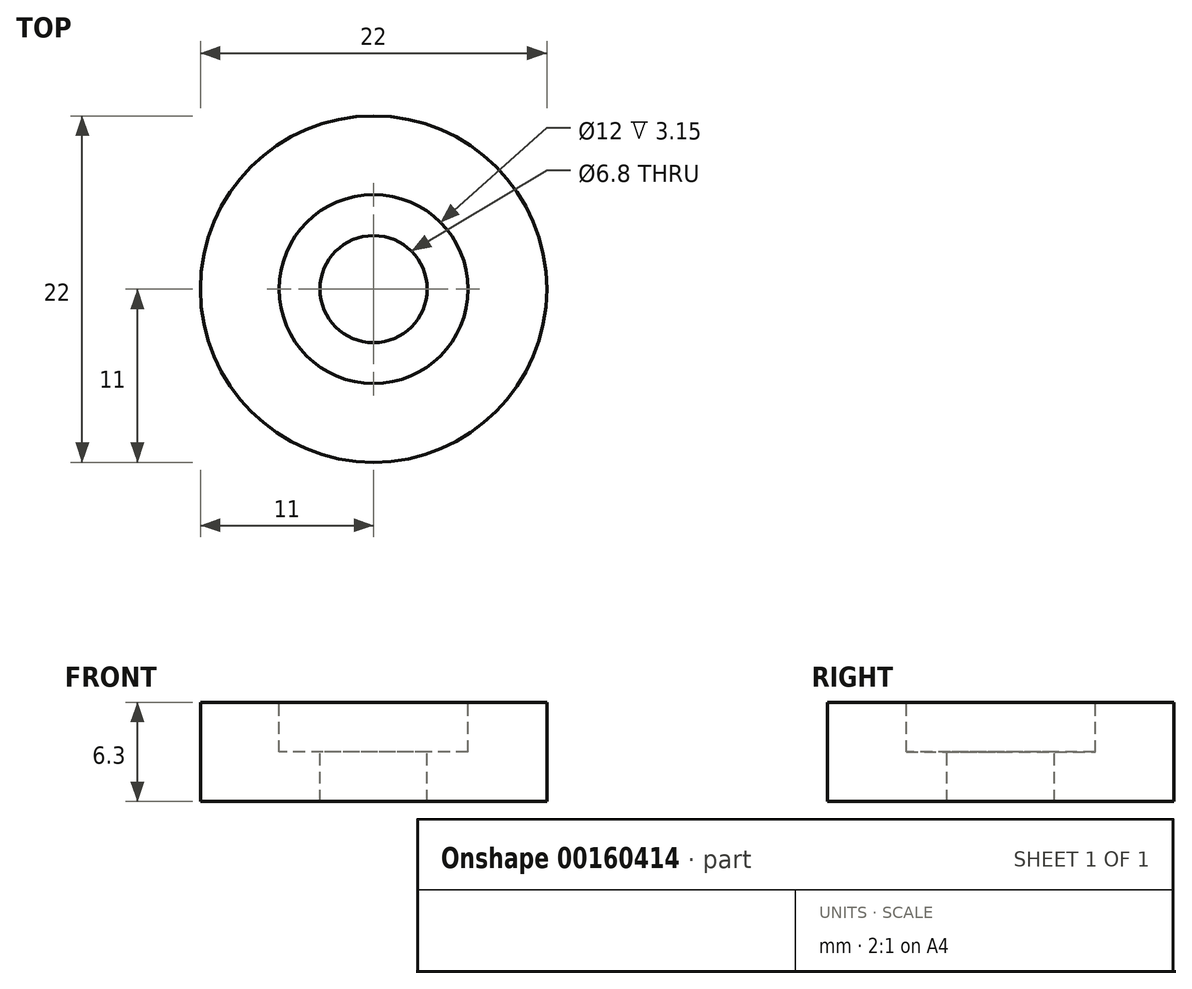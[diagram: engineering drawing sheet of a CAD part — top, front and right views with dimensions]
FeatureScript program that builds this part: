
annotation { "Feature Type Name" : "Feature", "Feature Type Description" : "" }
export const myFeature = defineFeature(function(context is Context, id is Id, definition is map)
    precondition{}
    {
        {
            var Q0;
            Q0=qCreatedBy(makeId("Top.planeOp"),FACE);
            var sketch = newSketch(context, id + "F0", { "sketchPlane" : qUnion([Q0])});
            skCircle(sketch, "E0", {"center": v(0, 0) * mm, "radius": 11 * mm});
            skSolve(sketch);
        }
        {
            var Q0;
            Q0=makeQuery(id+"F0.imprint","IMPRINT",FACE,{"disambiguationData":[TD([[makeQuery(id+"F0.imprint","IMPRINT",EDGE,{"derivedFrom":sQuery(id+"F0.wireOp",EDGE,"E0")}),1.0]])]});
            extrude(context, id + "F1", {"entities" : qUnion([Q0]), "depth" : 6.3 * mm});
        }
        {
            var Q0;
            Q0=makeQuery(id+"F1.opExtrude","CAP_FACE",FACE,{"disambiguationData":[OSD([sQuery(id+"F0.wireOp",EDGE,"E0")])],"isStart":false});
            var sketch = newSketch(context, id + "F2", { "sketchPlane" : qUnion([Q0])});
            skCircle(sketch, "E1", {"center": v(0, 0) * mm, "radius": 6 * mm});
            skSolve(sketch);
        }
        {
            var Q0;
            Q0 = qSketchRegion(id + "F2", true);
            extrude(context, id + "F3", {"entities" : qUnion([Q0]), "operationType" : NewBodyOperationType.REMOVE, "oppositeDirection" : true, "depth" : (6.3 / 2) * mm});
        }
        {
            var Q0;
            Q0=makeQuery(id+"F3.boolean.opBoolean","COPY",FACE,{"derivedFrom":makeQuery(id+"F3.opExtrude","CAP_FACE",FACE,{"disambiguationData":[OSD([sQuery(id+"F2.wireOp",EDGE,"E1")])],"isStart":false})});
            var sketch = newSketch(context, id + "F4", { "sketchPlane" : qUnion([Q0])});
            skCircle(sketch, "E2", {"center": v(0, 0) * mm, "radius": 3.4 * mm});
            skSolve(sketch);
        }
        {
            var Q0;
            Q0 = qSketchRegion(id + "F4", true);
            extrude(context, id + "F5", {"entities" : qUnion([Q0]), "operationType" : NewBodyOperationType.REMOVE, "endBound" : BoundingType.THROUGH_ALL, "oppositeDirection" : true, "depth" : 25 * mm});
        }
    });
